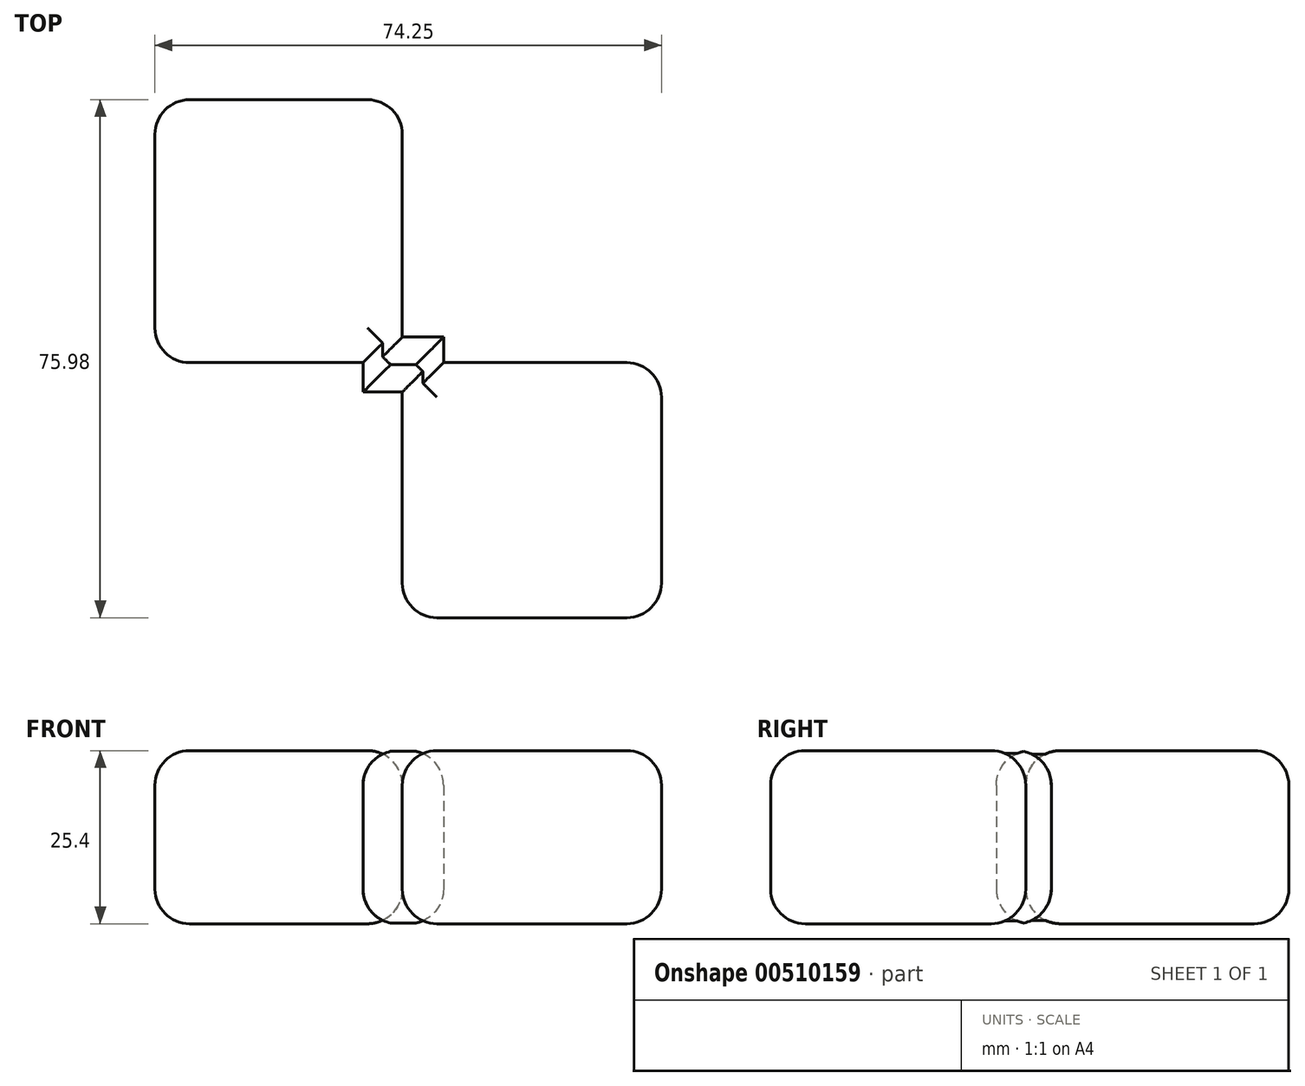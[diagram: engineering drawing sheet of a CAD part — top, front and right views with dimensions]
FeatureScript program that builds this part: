
annotation { "Feature Type Name" : "Feature", "Feature Type Description" : "" }
export const myFeature = defineFeature(function(context is Context, id is Id, definition is map)
    precondition{}
    {
        {
            var Q0;
            Q0=qCreatedBy(makeId("Top.planeOp"),FACE);
            var sketch = newSketch(context, id + "F0", { "sketchPlane" : qUnion([Q0])});
            skLineSegment(sketch, "E0.bottom", {"start": v(0, 0) * mm, "end": v(-36.26, 0) * mm});
            skLineSegment(sketch, "E0.top", {"start": v(0, 38.57) * mm, "end": v(-36.26, 38.57) * mm});
            skLineSegment(sketch, "E0.left", {"start": v(0, 0) * mm, "end": v(0, 38.57) * mm});
            skLineSegment(sketch, "E0.right", {"start": v(-36.26, 0) * mm, "end": v(-36.26, 38.57) * mm});
            skLineSegment(sketch, "E1.bottom", {"start": v(0, 0) * mm, "end": v(38, 0) * mm});
            skLineSegment(sketch, "E1.top", {"start": v(0, -37.41) * mm, "end": v(38, -37.41) * mm});
            skLineSegment(sketch, "E1.left", {"start": v(0, 0) * mm, "end": v(0, -37.41) * mm});
            skLineSegment(sketch, "E1.right", {"start": v(38, 0) * mm, "end": v(38, -37.41) * mm});
            skLineSegment(sketch, "E2.bottom", {"start": v(0, -19.47) * mm, "end": v(-25.96, -19.47) * mm});
            skLineSegment(sketch, "E2.left", {"start": v(0, -19.47) * mm, "end": v(0, 19.47) * mm});
            skLineSegment(sketch, "E2.right", {"start": v(-25.96, -19.47) * mm, "end": v(-25.96, 0) * mm});
            skPoint(sketch, "E2.middle", {"position": v(-12.98, 0) * mm});
            skPoint(sketch, "E2.top.end.orphan", {"position": v(-25.96, 19.47) * mm});
            skSolve(sketch);
        }
        {
            var Q0;
            Q0=makeQuery(id+"F0.imprint","IMPRINT",FACE,{"disambiguationData":[TD([[makeQuery(id+"F0.imprint","IMPRINT",EDGE,{"derivedFrom":sQuery(id+"F0.wireOp",EDGE,"E0.bottom")}),-1.0]])]});
            var Q1;
            Q1=makeQuery(id+"F0.imprint","IMPRINT",FACE,{"disambiguationData":[TD([[makeQuery(id+"F0.imprint","IMPRINT",EDGE,{"derivedFrom":sQuery(id+"F0.wireOp",EDGE,"E1.bottom")}),-1.0]])]});
            extrude(context, id + "F1", {"entities" : qUnion([Q0, Q1]), "depth" : 25.4 * mm, "offsetDistance" : 25.4 * mm});
        }
        {
            var Q0;
            Q0=qCreatedBy(makeId("Top.planeOp"),FACE);
            var sketch = newSketch(context, id + "F2", { "sketchPlane" : qUnion([Q0])});
            skLineSegment(sketch, "E3.bottom", {"start": v(0, 0) * mm, "end": v(-5.76, 0) * mm});
            skLineSegment(sketch, "E3.top", {"start": v(0, -4.32) * mm, "end": v(-5.76, -4.32) * mm});
            skLineSegment(sketch, "E3.left", {"start": v(0, 0) * mm, "end": v(0, -4.32) * mm});
            skLineSegment(sketch, "E3.right", {"start": v(-5.76, 0) * mm, "end": v(-5.76, -4.32) * mm});
            skLineSegment(sketch, "E4.bottom", {"start": v(0, 0) * mm, "end": v(6.04, 0) * mm});
            skLineSegment(sketch, "E4.top", {"start": v(0, 3.74) * mm, "end": v(6.04, 3.74) * mm});
            skLineSegment(sketch, "E4.left", {"start": v(0, 0) * mm, "end": v(0, 3.74) * mm});
            skLineSegment(sketch, "E4.right", {"start": v(6.04, 0) * mm, "end": v(6.04, 3.74) * mm});
            skSolve(sketch);
        }
        {
            var Q0;
            Q0=makeQuery(id+"F2.imprint","IMPRINT",FACE,{"disambiguationData":[TD([[makeQuery(id+"F2.imprint","IMPRINT",EDGE,{"derivedFrom":sQuery(id+"F2.wireOp",EDGE,"E3.bottom")}),1.0]])]});
            var Q1;
            Q1=makeQuery(id+"F2.imprint","IMPRINT",FACE,{"disambiguationData":[TD([[makeQuery(id+"F2.imprint","IMPRINT",EDGE,{"derivedFrom":sQuery(id+"F2.wireOp",EDGE,"E4.bottom")}),1.0]])]});
            extrude(context, id + "F3", {"entities" : qUnion([Q0, Q1]), "depth" : 25.4 * mm, "offsetDistance" : 25.4 * mm});
        }
        {
            var Q0;
            Q0=makeQuery(id+"F2.imprint","IMPRINT",FACE,{"disambiguationData":[TD([[makeQuery(id+"F2.imprint","IMPRINT",EDGE,{"derivedFrom":sQuery(id+"F2.wireOp",EDGE,"E3.bottom")}),1.0]])]});
            var Q1;
            Q1=makeQuery(id+"F2.imprint","IMPRINT",FACE,{"disambiguationData":[TD([[makeQuery(id+"F2.imprint","IMPRINT",EDGE,{"derivedFrom":sQuery(id+"F2.wireOp",EDGE,"E4.bottom")}),1.0]])]});
            extrude(context, id + "F4", {"entities" : qUnion([Q0, Q1]), "depth" : 25.4 * mm, "offsetDistance" : 25.4 * mm});
        }
        {
            var Q0;
            Q0=makeQuery(id+"F3.opExtrude","SWEPT_BODY",BODY,{"disambiguationData":[OSD([sQuery(id+"F2.wireOp",EDGE,"E4.bottom"),sQuery(id+"F2.wireOp",EDGE,"E4.top"),sQuery(id+"F2.wireOp",EDGE,"E4.left"),sQuery(id+"F2.wireOp",EDGE,"E4.right")])]});
            var Q1;
            Q1=makeQuery(id+"F1.opExtrude","SWEPT_BODY",BODY,{"disambiguationData":[OSD([sQuery(id+"F0.wireOp",EDGE,"E0.bottom"),sQuery(id+"F0.wireOp",EDGE,"E0.top"),sQuery(id+"F0.wireOp",EDGE,"E0.left"),sQuery(id+"F0.wireOp",EDGE,"E0.right"),sQuery(id+"F0.wireOp",EDGE,"E2.left")])]});
            var Q2;
            Q2=makeQuery(id+"F1.opExtrude","SWEPT_BODY",BODY,{"disambiguationData":[OSD([sQuery(id+"F0.wireOp",EDGE,"E1.bottom"),sQuery(id+"F0.wireOp",EDGE,"E1.top"),sQuery(id+"F0.wireOp",EDGE,"E1.left"),sQuery(id+"F0.wireOp",EDGE,"E1.right"),sQuery(id+"F0.wireOp",EDGE,"E2.left")])]});
            var Q3;
            Q3=makeQuery(id+"F3.opExtrude","SWEPT_BODY",BODY,{"disambiguationData":[OSD([sQuery(id+"F2.wireOp",EDGE,"E3.bottom"),sQuery(id+"F2.wireOp",EDGE,"E3.top"),sQuery(id+"F2.wireOp",EDGE,"E3.left"),sQuery(id+"F2.wireOp",EDGE,"E3.right")])]});
            var Q4;
            Q4=makeQuery(id+"F4.opExtrude","SWEPT_BODY",BODY,{"disambiguationData":[OSD([sQuery(id+"F2.wireOp",EDGE,"E4.bottom"),sQuery(id+"F2.wireOp",EDGE,"E4.top"),sQuery(id+"F2.wireOp",EDGE,"E4.left"),sQuery(id+"F2.wireOp",EDGE,"E4.right")])]});
            var Q5;
            Q5=makeQuery(id+"F4.opExtrude","SWEPT_BODY",BODY,{"disambiguationData":[OSD([sQuery(id+"F2.wireOp",EDGE,"E3.bottom"),sQuery(id+"F2.wireOp",EDGE,"E3.top"),sQuery(id+"F2.wireOp",EDGE,"E3.left"),sQuery(id+"F2.wireOp",EDGE,"E3.right")])]});
            booleanBodies(context, id + "F5", {"operationType" : BooleanOperationType.UNION, "tools" : qUnion([Q0, Q1, Q2, Q3, Q4, Q5])});
        }
        {
            var Q0;
            {var subQ0=sQuery(id+"F2.wireOp",EDGE,"E4.right");var subQ1=sQuery(id+"F2.wireOp",EDGE,"E4.left");var subQ2=sQuery(id+"F2.wireOp",EDGE,"E4.top");var subQ3=sQuery(id+"F2.wireOp",EDGE,"E4.bottom");var subQ4=sQuery(id+"F0.wireOp",EDGE,"E2.left");Q0=makeQuery(id+"F5.opBoolean","MERGE",FACE,{"derivedFrom":[makeQuery(id+"F1.opExtrude","CAP_FACE",FACE,{"disambiguationData":[OSD([sQuery(id+"F0.wireOp",EDGE,"E0.bottom"),sQuery(id+"F0.wireOp",EDGE,"E0.top"),sQuery(id+"F0.wireOp",EDGE,"E0.left"),sQuery(id+"F0.wireOp",EDGE,"E0.right"),subQ4])],"isStart":false}),makeQuery(id+"F1.opExtrude","CAP_FACE",FACE,{"disambiguationData":[OSD([sQuery(id+"F0.wireOp",EDGE,"E1.bottom"),sQuery(id+"F0.wireOp",EDGE,"E1.top"),sQuery(id+"F0.wireOp",EDGE,"E1.left"),sQuery(id+"F0.wireOp",EDGE,"E1.right"),subQ4])],"isStart":false}),makeQuery(id+"F3.opExtrude","CAP_FACE",FACE,{"disambiguationData":[OSD([sQuery(id+"F2.wireOp",EDGE,"E3.bottom"),sQuery(id+"F2.wireOp",EDGE,"E3.top"),sQuery(id+"F2.wireOp",EDGE,"E3.left"),sQuery(id+"F2.wireOp",EDGE,"E3.right")])],"isStart":false}),makeQuery(id+"F3.opExtrude","CAP_FACE",FACE,{"disambiguationData":[OSD([subQ3,subQ2,subQ1,subQ0])],"isStart":false}),makeQuery(id+"F4.opExtrude","CAP_FACE",FACE,{"disambiguationData":[OSD([subQ3,subQ2,subQ1,subQ0])],"isStart":false})]});}
            var Q1;
            {var subQ0=sQuery(id+"F2.wireOp",EDGE,"E4.right");var subQ1=sQuery(id+"F2.wireOp",EDGE,"E4.left");var subQ2=sQuery(id+"F2.wireOp",EDGE,"E4.top");var subQ3=sQuery(id+"F2.wireOp",EDGE,"E4.bottom");var subQ4=sQuery(id+"F0.wireOp",EDGE,"E2.left");Q1=makeQuery(id+"F5.opBoolean","MERGE",FACE,{"derivedFrom":[makeQuery(id+"F1.opExtrude","CAP_FACE",FACE,{"disambiguationData":[OSD([sQuery(id+"F0.wireOp",EDGE,"E0.bottom"),sQuery(id+"F0.wireOp",EDGE,"E0.top"),sQuery(id+"F0.wireOp",EDGE,"E0.left"),sQuery(id+"F0.wireOp",EDGE,"E0.right"),subQ4])],"isStart":true}),makeQuery(id+"F1.opExtrude","CAP_FACE",FACE,{"disambiguationData":[OSD([sQuery(id+"F0.wireOp",EDGE,"E1.bottom"),sQuery(id+"F0.wireOp",EDGE,"E1.top"),sQuery(id+"F0.wireOp",EDGE,"E1.left"),sQuery(id+"F0.wireOp",EDGE,"E1.right"),subQ4])],"isStart":true}),makeQuery(id+"F3.opExtrude","CAP_FACE",FACE,{"disambiguationData":[OSD([sQuery(id+"F2.wireOp",EDGE,"E3.bottom"),sQuery(id+"F2.wireOp",EDGE,"E3.top"),sQuery(id+"F2.wireOp",EDGE,"E3.left"),sQuery(id+"F2.wireOp",EDGE,"E3.right")])],"isStart":true}),makeQuery(id+"F3.opExtrude","CAP_FACE",FACE,{"disambiguationData":[OSD([subQ3,subQ2,subQ1,subQ0])],"isStart":true}),makeQuery(id+"F4.opExtrude","CAP_FACE",FACE,{"disambiguationData":[OSD([subQ3,subQ2,subQ1,subQ0])],"isStart":true})]});}
            fillet(context, id + "F6", {"entities" : qUnion([Q0, Q1]), "radius" : 5.08 * mm, "tangentPropagation" : true, "allowEdgeOverflow" : false});
        }
        {
            var Q0;
            Q0=makeQuery(id+"F1.opExtrude","SWEPT_EDGE",EDGE,{"disambiguationData":[OSD([sQuery(id+"F0.wireOp",EDGE,"E0.top"),sQuery(id+"F0.wireOp",EDGE,"E0.left")])]});
            var Q1;
            {var subQ0=sQuery(id+"F2.wireOp",EDGE,"E4.left");var subQ1=sQuery(id+"F2.wireOp",EDGE,"E4.top");Q1=makeQuery(id+"F5.opBoolean","MERGE",EDGE,{"derivedFrom":[makeQuery(id+"F3.opExtrude","SWEPT_EDGE",EDGE,{"disambiguationData":[OSD([subQ1,subQ0])]}),makeQuery(id+"F4.opExtrude","SWEPT_EDGE",EDGE,{"disambiguationData":[OSD([subQ1,subQ0])]})]});}
            var Q2;
            Q2=makeQuery(id+"F1.opExtrude","SWEPT_EDGE",EDGE,{"disambiguationData":[OSD([sQuery(id+"F0.wireOp",EDGE,"E1.bottom"),sQuery(id+"F0.wireOp",EDGE,"E1.right")])]});
            var Q3;
            Q3=makeQuery(id+"F1.opExtrude","SWEPT_EDGE",EDGE,{"disambiguationData":[OSD([sQuery(id+"F0.wireOp",EDGE,"E1.top"),sQuery(id+"F0.wireOp",EDGE,"E1.right")])]});
            var Q4;
            Q4=makeQuery(id+"F1.opExtrude","SWEPT_EDGE",EDGE,{"disambiguationData":[OSD([sQuery(id+"F0.wireOp",EDGE,"E1.top"),sQuery(id+"F0.wireOp",EDGE,"E1.left")])]});
            var Q5;
            Q5=makeQuery(id+"F3.opExtrude","SWEPT_EDGE",EDGE,{"disambiguationData":[OSD([sQuery(id+"F2.wireOp",EDGE,"E3.top"),sQuery(id+"F2.wireOp",EDGE,"E3.left")])]});
            var Q6;
            Q6=makeQuery(id+"F1.opExtrude","SWEPT_EDGE",EDGE,{"disambiguationData":[OSD([sQuery(id+"F0.wireOp",EDGE,"E0.bottom"),sQuery(id+"F0.wireOp",EDGE,"E0.right")])]});
            var Q7;
            Q7=makeQuery(id+"F1.opExtrude","SWEPT_EDGE",EDGE,{"disambiguationData":[OSD([sQuery(id+"F0.wireOp",EDGE,"E0.top"),sQuery(id+"F0.wireOp",EDGE,"E0.right")])]});
            fillet(context, id + "F7", {"entities" : qUnion([Q0, Q1, Q2, Q3, Q4, Q5, Q6, Q7]), "radius" : 5.08 * mm, "tangentPropagation" : true, "allowEdgeOverflow" : false});
        }
        {
            var Q0;
            {var subQ0=sQuery(id+"F2.wireOp",EDGE,"E4.right");var subQ1=sQuery(id+"F2.wireOp",EDGE,"E4.left");var subQ2=sQuery(id+"F2.wireOp",EDGE,"E4.top");var subQ3=sQuery(id+"F2.wireOp",EDGE,"E4.bottom");var subQ4=sQuery(id+"F0.wireOp",EDGE,"E2.left");Q0=makeQuery(id+"F6.opFillet","SPLIT",FACE,{"disambiguationData":[OD(0.0)],"derivedFrom":makeQuery(id+"F5.opBoolean","MERGE",FACE,{"derivedFrom":[makeQuery(id+"F1.opExtrude","CAP_FACE",FACE,{"disambiguationData":[OSD([sQuery(id+"F0.wireOp",EDGE,"E0.bottom"),sQuery(id+"F0.wireOp",EDGE,"E0.top"),sQuery(id+"F0.wireOp",EDGE,"E0.left"),sQuery(id+"F0.wireOp",EDGE,"E0.right"),subQ4])],"isStart":false}),makeQuery(id+"F1.opExtrude","CAP_FACE",FACE,{"disambiguationData":[OSD([sQuery(id+"F0.wireOp",EDGE,"E1.bottom"),sQuery(id+"F0.wireOp",EDGE,"E1.top"),sQuery(id+"F0.wireOp",EDGE,"E1.left"),sQuery(id+"F0.wireOp",EDGE,"E1.right"),subQ4])],"isStart":false}),makeQuery(id+"F3.opExtrude","CAP_FACE",FACE,{"disambiguationData":[OSD([sQuery(id+"F2.wireOp",EDGE,"E3.bottom"),sQuery(id+"F2.wireOp",EDGE,"E3.top"),sQuery(id+"F2.wireOp",EDGE,"E3.left"),sQuery(id+"F2.wireOp",EDGE,"E3.right")])],"isStart":false}),makeQuery(id+"F3.opExtrude","CAP_FACE",FACE,{"disambiguationData":[OSD([subQ3,subQ2,subQ1,subQ0])],"isStart":false}),makeQuery(id+"F4.opExtrude","CAP_FACE",FACE,{"disambiguationData":[OSD([subQ3,subQ2,subQ1,subQ0])],"isStart":false})]})});}
            var sketch = newSketch(context, id + "F8", { "sketchPlane" : qUnion([Q0])});
            skFitSpline(sketch, "E5", {"points": [v(-24.37, 16.78) * mm, v(-21.04, 27.23) * mm, v(-13.49, 21.73) * mm, v(-16.57, 12.29) * mm, v(-24.37, 16.78) * mm]});
            skSolve(sketch);
        }
        {
            var Q0;
            Q0=makeQuery(id+"F8.imprint","IMPRINT",FACE,{"disambiguationData":[TD([[makeQuery(id+"F8.imprint","IMPRINT",EDGE,{"derivedFrom":sQuery(id+"F8.wireOp",EDGE,"E5")}),-1.0]])]});
            extrude(context, id + "F9", {"entities" : qUnion([Q0]), "operationType" : NewBodyOperationType.ADD, "oppositeDirection" : true, "depth" : 2.03 * mm, "offsetDistance" : 25.4 * mm});
        }
    });
